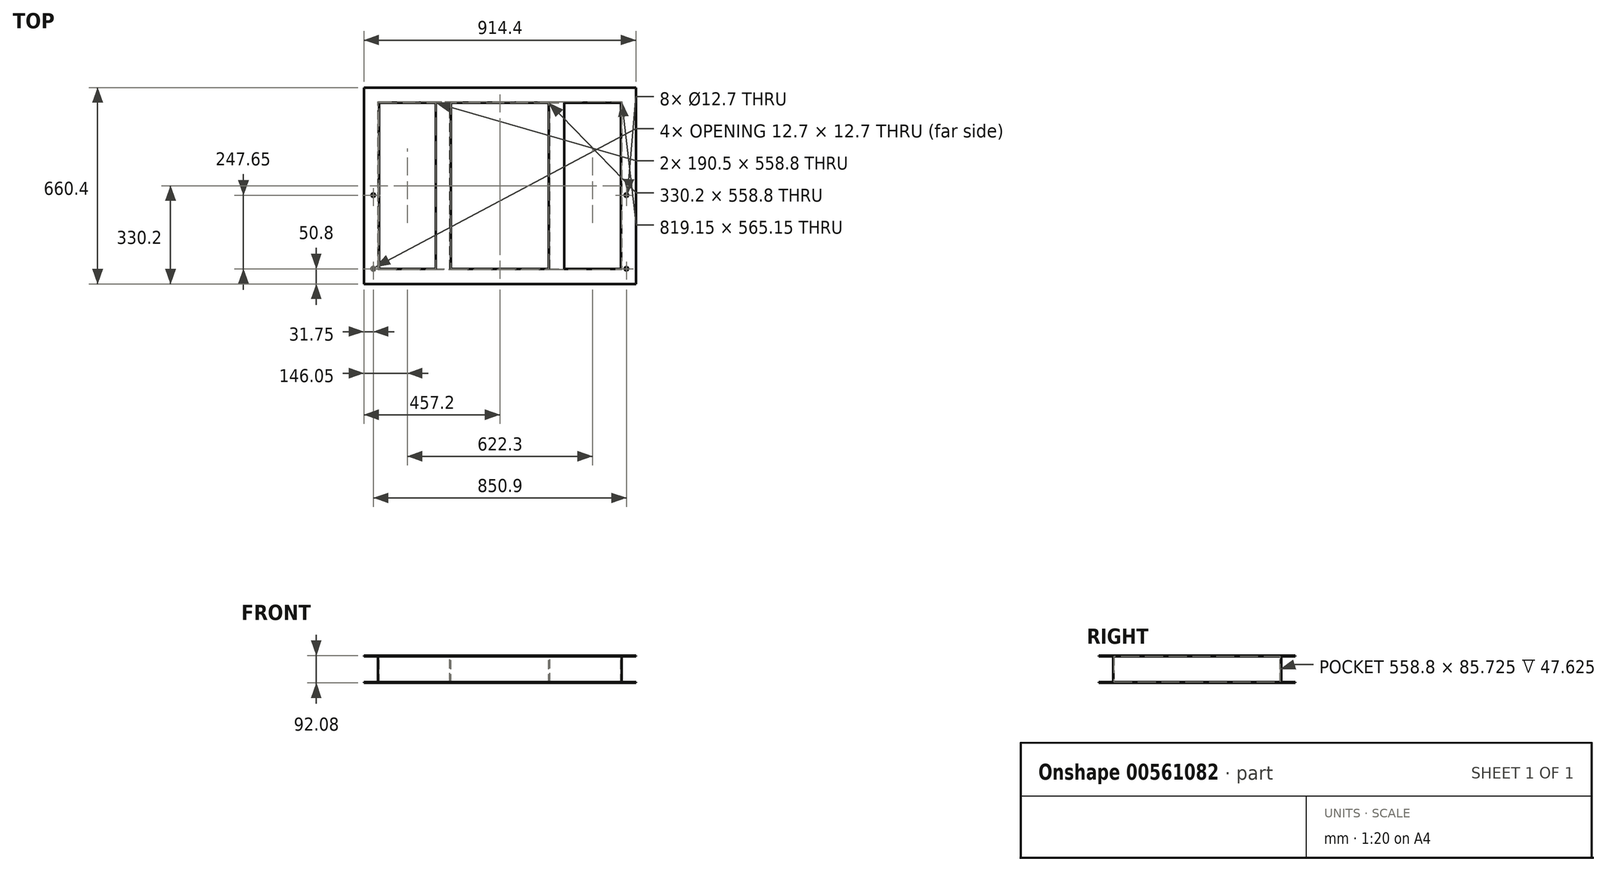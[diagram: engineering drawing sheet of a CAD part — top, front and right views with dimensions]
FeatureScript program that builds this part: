
annotation { "Feature Type Name" : "Feature", "Feature Type Description" : "" }
export const myFeature = defineFeature(function(context is Context, id is Id, definition is map)
    precondition{}
    {
        {
            var Q0;
            Q0=qCreatedBy(makeId("Top.planeOp"),FACE);
            var sketch = newSketch(context, id + "F0", { "sketchPlane" : qUnion([Q0])});
            skLineSegment(sketch, "E0", {"start": v(406.4, 279.4) * mm, "end": v(-406.4, 279.4) * mm});
            skLineSegment(sketch, "E1", {"start": v(-406.4, 279.4) * mm, "end": v(-406.4, -279.4) * mm});
            skLineSegment(sketch, "E2", {"start": v(-406.4, -279.4) * mm, "end": v(406.4, -279.4) * mm});
            skLineSegment(sketch, "E3", {"start": v(406.4, -279.4) * mm, "end": v(406.4, 279.4) * mm});
            skSolve(sketch);
        }
        {
            var Q0;
            Q0=qCreatedBy(makeId("Front.planeOp"),FACE);
            var sketch = newSketch(context, id + "F1", { "sketchPlane" : qUnion([Q0])});
            skLineSegment(sketch, "E4", {"start": v(406.4, 0) * mm, "end": v(406.4, 46.04) * mm});
            skLineSegment(sketch, "E5", {"start": v(457.2, 46.04) * mm, "end": v(406.4, 46.04) * mm});
            skLineSegment(sketch, "E6", {"start": v(406.4, -46.04) * mm, "end": v(457.2, -46.04) * mm});
            skLineSegment(sketch, "E7", {"start": v(406.4, -46.04) * mm, "end": v(406.4, 0) * mm});
            skLineSegment(sketch, "E8", {"start": v(457.2, 46.04) * mm, "end": v(457.2, 42.86) * mm});
            skLineSegment(sketch, "E9", {"start": v(409.58, 42.86) * mm, "end": v(457.2, 42.86) * mm});
            skLineSegment(sketch, "E10", {"start": v(409.58, 42.86) * mm, "end": v(409.58, -42.86) * mm});
            skLineSegment(sketch, "E11", {"start": v(457.2, -42.86) * mm, "end": v(409.58, -42.86) * mm});
            skLineSegment(sketch, "E12", {"start": v(457.2, -42.86) * mm, "end": v(457.2, -46.04) * mm});
            skSolve(sketch);
        }
        {
            var Q0;
            Q0 = qSketchRegion(id + "F1", true);
            var Q1;
            Q1 = qConstructionFilter(qBodyType(qCreatedBy(id + "F0" ,EDGE), BodyType.WIRE), ConstructionObject.NO);
            sweep(context, id + "F2", {"profiles" : qUnion([Q0]), "path" : qUnion([Q1])});
        }
        {
            var Q0;
            Q0=makeQuery(id+"F2.opSweep","SWEPT_FACE",FACE,{"disambiguationData":[OSD([sQuery(id+"F0.wireOp",EDGE,"E0"),sQuery(id+"F1.wireOp",EDGE,"E4"),sQuery(id+"F1.wireOp",EDGE,"E7")])]});
            var sketch = newSketch(context, id + "F3", { "sketchPlane" : qUnion([Q0])});
            skLineSegment(sketch, "E13", {"start": v(-215.9, 46.04) * mm, "end": v(-165.1, 46.04) * mm});
            skLineSegment(sketch, "E14", {"start": v(-165.1, 46.04) * mm, "end": v(-165.1, -46.04) * mm});
            skLineSegment(sketch, "E15", {"start": v(-165.1, -46.04) * mm, "end": v(-215.9, -46.04) * mm});
            skLineSegment(sketch, "E16", {"start": v(-215.9, -46.04) * mm, "end": v(-215.9, -42.86) * mm});
            skLineSegment(sketch, "E17", {"start": v(-215.9, -42.86) * mm, "end": v(-168.28, -42.86) * mm});
            skLineSegment(sketch, "E18", {"start": v(-168.28, -42.86) * mm, "end": v(-168.28, 42.86) * mm});
            skLineSegment(sketch, "E19", {"start": v(-168.28, 42.86) * mm, "end": v(-215.9, 42.86) * mm});
            skLineSegment(sketch, "E20", {"start": v(-215.9, 42.86) * mm, "end": v(-215.9, 46.04) * mm});
            skLineSegment(sketch, "E21.MirrorCS", {"start": v(215.9, -46.04) * mm, "end": v(215.9, -42.86) * mm});
            skLineSegment(sketch, "E22.MirrorCS", {"start": v(215.9, 42.86) * mm, "end": v(215.9, 46.04) * mm});
            skLineSegment(sketch, "E23.MirrorCS", {"start": v(165.1, -46.04) * mm, "end": v(215.9, -46.04) * mm});
            skLineSegment(sketch, "E24.MirrorCS", {"start": v(165.1, 46.04) * mm, "end": v(165.1, -46.04) * mm});
            skLineSegment(sketch, "E25.MirrorCS", {"start": v(215.9, -42.86) * mm, "end": v(168.28, -42.86) * mm});
            skLineSegment(sketch, "E26.MirrorCS", {"start": v(168.28, -42.86) * mm, "end": v(168.28, 42.86) * mm});
            skLineSegment(sketch, "E27.MirrorCS", {"start": v(168.28, 42.86) * mm, "end": v(215.9, 42.86) * mm});
            skLineSegment(sketch, "E28.MirrorCS", {"start": v(215.9, 46.04) * mm, "end": v(165.1, 46.04) * mm});
            skSolve(sketch);
        }
        {
            var Q0;
            Q0 = qSketchRegion(id + "F3", true);
            var Q1;
            Q1=makeQuery(id+"F2.opSweep","SWEPT_FACE",FACE,{"disambiguationData":[OSD([sQuery(id+"F0.wireOp",EDGE,"E2"),sQuery(id+"F1.wireOp",EDGE,"E4"),sQuery(id+"F1.wireOp",EDGE,"E7")])]});
            extrude(context, id + "F4", {"entities" : qUnion([Q0]), "operationType" : NewBodyOperationType.ADD, "endBound" : BoundingType.UP_TO_SURFACE, "depth" : 25.4 * mm, "endBoundEntityFace" : qUnion([Q1]), "offsetDistance" : 25.4 * mm});
        }
        {
            var Q0;
            Q0=makeQuery(id+"F4.boolean.opBoolean","MERGE",FACE,{"derivedFrom":[makeQuery(id+"F2.opSweep","SWEPT_FACE",FACE,{"disambiguationData":[OSD([sQuery(id+"F0.wireOp",EDGE,"E3"),sQuery(id+"F1.wireOp",EDGE,"E5")])]}),makeQuery(id+"F4.opExtrude","SWEPT_FACE",FACE,{"disambiguationData":[OSD([sQuery(id+"F3.wireOp",EDGE,"E13")])]}),makeQuery(id+"F4.opExtrude","SWEPT_FACE",FACE,{"disambiguationData":[OSD([sQuery(id+"F3.wireOp",EDGE,"E28.MirrorCS")])]})]});
            var sketch = newSketch(context, id + "F5", { "sketchPlane" : qUnion([Q0])});
            skCircle(sketch, "E29", {"center": v(-425.45, -279.4) * mm, "radius": 6.35 * mm});
            skCircle(sketch, "E30", {"center": v(-425.45, -31.75) * mm, "radius": 6.35 * mm});
            skCircle(sketch, "E31", {"center": v(425.45, -279.4) * mm, "radius": 6.35 * mm});
            skCircle(sketch, "E32", {"center": v(425.45, -31.75) * mm, "radius": 6.35 * mm});
            skSolve(sketch);
        }
        {
            var Q0;
            Q0 = qSketchRegion(id + "F5", true);
            extrude(context, id + "F6", {"entities" : qUnion([Q0]), "operationType" : NewBodyOperationType.REMOVE, "endBound" : BoundingType.THROUGH_ALL, "oppositeDirection" : true, "depth" : 25.4 * mm, "offsetDistance" : 25.4 * mm});
        }
    });
